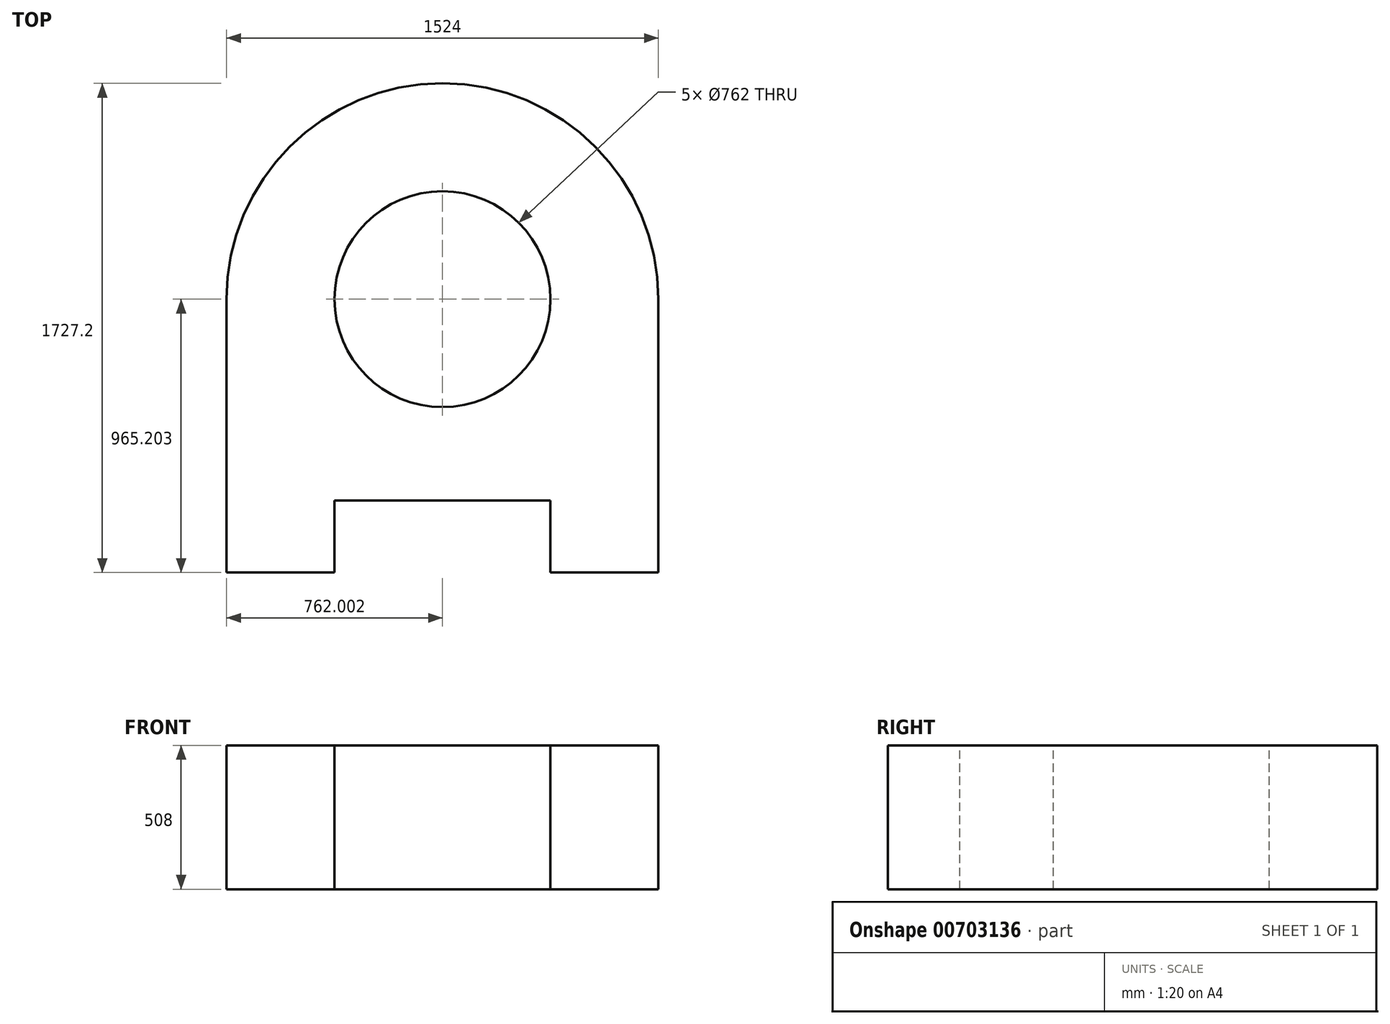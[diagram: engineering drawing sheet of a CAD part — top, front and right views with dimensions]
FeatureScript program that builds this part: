
annotation { "Feature Type Name" : "Feature", "Feature Type Description" : "" }
export const myFeature = defineFeature(function(context is Context, id is Id, definition is map)
    precondition{}
    {
        {
            var Q0;
            Q0=qCreatedBy(makeId("Top.planeOp"),FACE);
            var sketch = newSketch(context, id + "F0", { "sketchPlane" : qUnion([Q0])});
            skLineSegment(sketch, "E0.bottom", {"start": v(524.82, 191.52) * mm, "end": v(-999.18, 191.52) * mm});
            skLineSegment(sketch, "E0.top", {"start": v(524.82, -773.68) * mm, "end": v(143.82, -773.68) * mm});
            skLineSegment(sketch, "E0.left", {"start": v(524.82, 191.52) * mm, "end": v(524.82, -773.68) * mm});
            skLineSegment(sketch, "E0.right", {"start": v(-999.18, 191.52) * mm, "end": v(-999.18, -773.68) * mm});
            skPoint(sketch, "E1", {"position": v(0, 191.52) * mm});
            skPoint(sketch, "E2", {"position": v(-618.18, -773.68) * mm});
            skPoint(sketch, "E3", {"position": v(143.82, -773.68) * mm});
            skLineSegment(sketch, "E4", {"start": v(-618.18, -773.68) * mm, "end": v(-999.18, -773.68) * mm});
            skLineSegment(sketch, "E5", {"start": v(143.82, -773.68) * mm, "end": v(524.82, -773.68) * mm});
            skLineSegment(sketch, "E6", {"start": v(-618.18, -773.68) * mm, "end": v(-618.18, -519.68) * mm});
            skLineSegment(sketch, "E7", {"start": v(143.82, -773.68) * mm, "end": v(143.82, -519.68) * mm});
            skLineSegment(sketch, "E8", {"start": v(-618.18, -519.68) * mm, "end": v(143.82, -519.68) * mm});
            skArc(sketch, "E9", {"start": v(524.82, 191.52) * mm, "mid": v(-237.18, 953.52) * mm, "end": v(-999.18, 191.52) * mm});
            skCircle(sketch, "E10", {"center": v(-237.18, 191.52) * mm, "radius": 381 * mm});
            skSolve(sketch);
        }
        {
            var Q0;
            Q0=makeQuery(id+"F0.imprint","IMPRINT",FACE,{"disambiguationData":[TD([[makeQuery(id+"F0.imprint","IMPRINT",EDGE,{"derivedFrom":sQuery(id+"F0.wireOp",EDGE,"E0.bottom")}),1.0]])]});
            var sketch = newSketch(context, id + "F1", { "sketchPlane" : qUnion([Q0])});
            skSolve(sketch);
        }
        {
            var Q0;
            Q0=makeQuery(id+"F0.imprint","IMPRINT",FACE,{"disambiguationData":[TD([[makeQuery(id+"F0.imprint","IMPRINT",EDGE,{"derivedFrom":sQuery(id+"F0.wireOp",EDGE,"E0.bottom")}),1.0]])]});
            var Q1;
            {var subQ0=sQuery(id+"F0.wireOp",EDGE,"E9");Q1=makeQuery(id+"F0.imprint","IMPRINT",FACE,{"disambiguationData":[TD([[makeQuery(id+"F0.imprint","IMPRINT",EDGE,{"derivedFrom":subQ0}),1.0]])]});}
            extrude(context, id + "F2", {"entities" : qUnion([Q0, Q1]), "oppositeDirection" : true, "depth" : 508 * mm, "offsetDistance" : 25.4 * mm});
        }
    });
